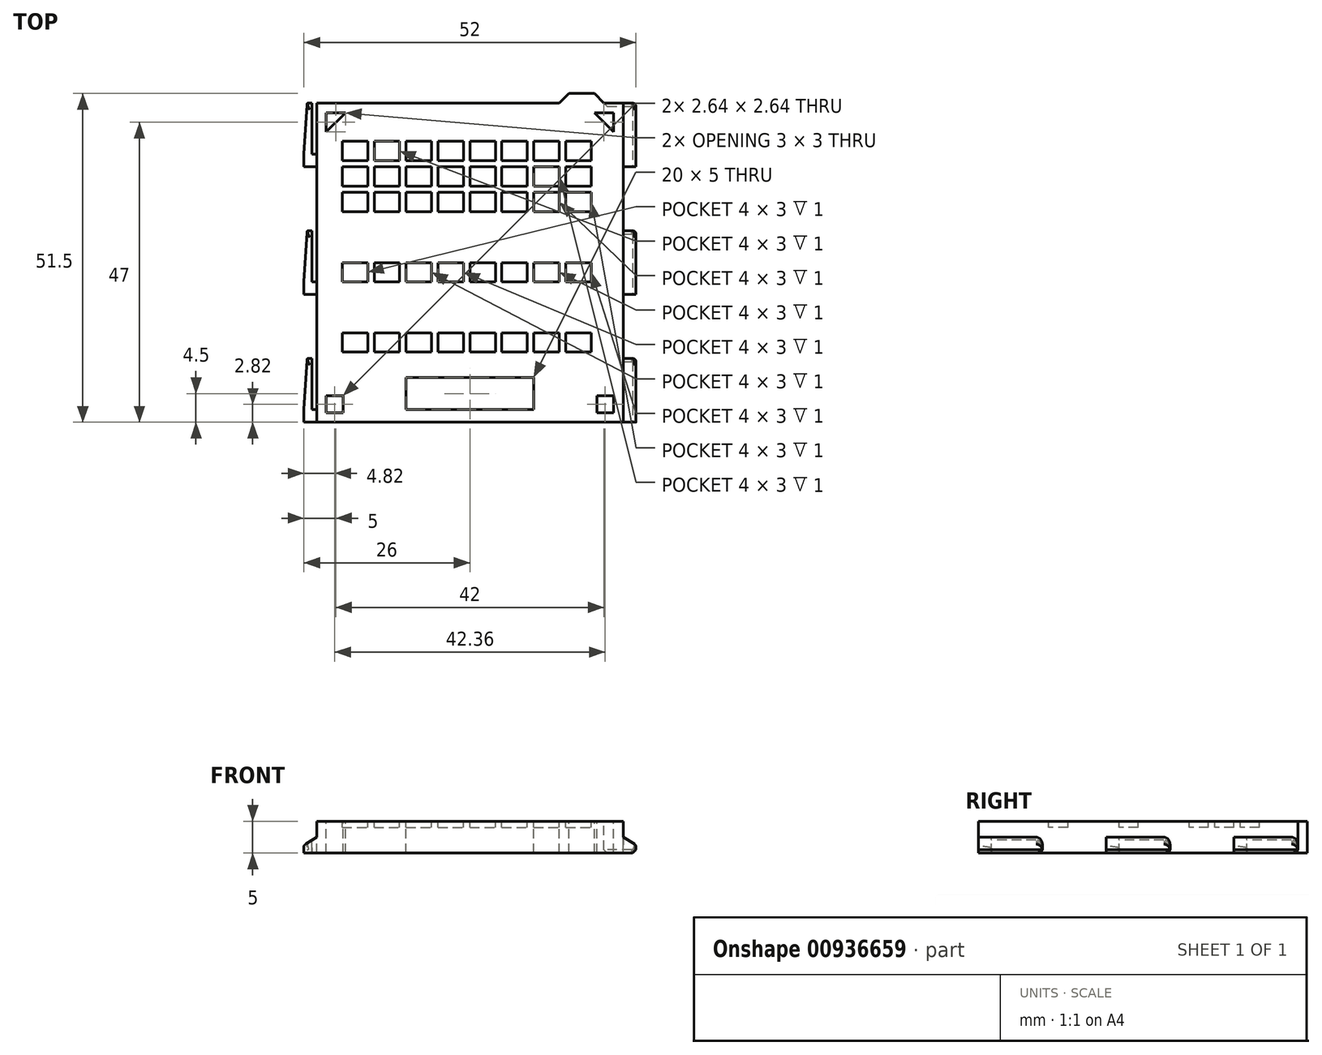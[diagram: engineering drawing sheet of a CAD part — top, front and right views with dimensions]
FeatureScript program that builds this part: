
annotation { "Feature Type Name" : "Feature", "Feature Type Description" : "" }
export const myFeature = defineFeature(function(context is Context, id is Id, definition is map)
    precondition{}
    {
        {
            var Q0;
            Q0=qCreatedBy(makeId("Top.planeOp"),FACE);
            var sketch = newSketch(context, id + "F0", { "sketchPlane" : qUnion([Q0])});
            skLineSegment(sketch, "E0.bottom", {"start": v(0, 0) * mm, "end": v(48, 0) * mm});
            skLineSegment(sketch, "E0.top", {"start": v(0, -50) * mm, "end": v(48, -50) * mm});
            skLineSegment(sketch, "E0.left", {"start": v(0, 0) * mm, "end": v(0, -50) * mm});
            skLineSegment(sketch, "E0.right", {"start": v(48, 0) * mm, "end": v(48, -50) * mm});
            skSolve(sketch);
        }
        {
            var Q0;
            Q0=makeQuery(id+"F0.imprint","IMPRINT",FACE,{"disambiguationData":[TD([[makeQuery(id+"F0.imprint","IMPRINT",EDGE,{"derivedFrom":sQuery(id+"F0.wireOp",EDGE,"E0.bottom")}),-1.0]])]});
            extrude(context, id + "F1", {"entities" : qUnion([Q0]), "depth" : 5 * mm, "offsetDistance" : 25 * mm});
        }
        {
            var Q0;
            Q0=makeQuery(id+"F1.opExtrude","CAP_FACE",FACE,{"disambiguationData":[OSD([sQuery(id+"F0.wireOp",EDGE,"E0.bottom"),sQuery(id+"F0.wireOp",EDGE,"E0.top"),sQuery(id+"F0.wireOp",EDGE,"E0.left"),sQuery(id+"F0.wireOp",EDGE,"E0.right")])],"isStart":false});
            var sketch = newSketch(context, id + "F2", { "sketchPlane" : qUnion([Q0])});
            skLineSegment(sketch, "E1.bottom", {"start": v(4, -6) * mm, "end": v(8, -6) * mm});
            skLineSegment(sketch, "E1.top", {"start": v(4, -9) * mm, "end": v(8, -9) * mm});
            skLineSegment(sketch, "E1.left", {"start": v(4, -6) * mm, "end": v(4, -9) * mm});
            skLineSegment(sketch, "E1.right", {"start": v(8, -6) * mm, "end": v(8, -9) * mm});
            skLineSegment(sketch, "E2.0.1.0", {"start": v(4, -13) * mm, "end": v(8, -13) * mm});
            skLineSegment(sketch, "E2.0.1.1", {"start": v(8, -10) * mm, "end": v(8, -13) * mm});
            skLineSegment(sketch, "E2.0.1.2", {"start": v(4, -10) * mm, "end": v(4, -13) * mm});
            skLineSegment(sketch, "E2.0.1.3", {"start": v(4, -10) * mm, "end": v(8, -10) * mm});
            skLineSegment(sketch, "E2.0.2.0", {"start": v(4, -17) * mm, "end": v(8, -17) * mm});
            skLineSegment(sketch, "E2.0.2.1", {"start": v(8, -14) * mm, "end": v(8, -17) * mm});
            skLineSegment(sketch, "E2.0.2.2", {"start": v(4, -14) * mm, "end": v(4, -17) * mm});
            skLineSegment(sketch, "E2.0.2.3", {"start": v(4, -14) * mm, "end": v(8, -14) * mm});
            skLineSegment(sketch, "E2.1.0.0", {"start": v(9, -9) * mm, "end": v(13, -9) * mm});
            skLineSegment(sketch, "E2.1.0.1", {"start": v(13, -6) * mm, "end": v(13, -9) * mm});
            skLineSegment(sketch, "E2.1.0.2", {"start": v(9, -6) * mm, "end": v(9, -9) * mm});
            skLineSegment(sketch, "E2.1.0.3", {"start": v(9, -6) * mm, "end": v(13, -6) * mm});
            skLineSegment(sketch, "E2.1.1.0", {"start": v(9, -13) * mm, "end": v(13, -13) * mm});
            skLineSegment(sketch, "E2.1.1.1", {"start": v(13, -10) * mm, "end": v(13, -13) * mm});
            skLineSegment(sketch, "E2.1.1.2", {"start": v(9, -10) * mm, "end": v(9, -13) * mm});
            skLineSegment(sketch, "E2.1.1.3", {"start": v(9, -10) * mm, "end": v(13, -10) * mm});
            skLineSegment(sketch, "E2.1.2.0", {"start": v(9, -17) * mm, "end": v(13, -17) * mm});
            skLineSegment(sketch, "E2.1.2.1", {"start": v(13, -14) * mm, "end": v(13, -17) * mm});
            skLineSegment(sketch, "E2.1.2.2", {"start": v(9, -14) * mm, "end": v(9, -17) * mm});
            skLineSegment(sketch, "E2.1.2.3", {"start": v(9, -14) * mm, "end": v(13, -14) * mm});
            skLineSegment(sketch, "E2.2.0.0", {"start": v(14, -9) * mm, "end": v(18, -9) * mm});
            skLineSegment(sketch, "E2.2.0.1", {"start": v(18, -6) * mm, "end": v(18, -9) * mm});
            skLineSegment(sketch, "E2.2.0.2", {"start": v(14, -6) * mm, "end": v(14, -9) * mm});
            skLineSegment(sketch, "E2.2.0.3", {"start": v(14, -6) * mm, "end": v(18, -6) * mm});
            skLineSegment(sketch, "E2.2.1.0", {"start": v(14, -13) * mm, "end": v(18, -13) * mm});
            skLineSegment(sketch, "E2.2.1.1", {"start": v(18, -10) * mm, "end": v(18, -13) * mm});
            skLineSegment(sketch, "E2.2.1.2", {"start": v(14, -10) * mm, "end": v(14, -13) * mm});
            skLineSegment(sketch, "E2.2.1.3", {"start": v(14, -10) * mm, "end": v(18, -10) * mm});
            skLineSegment(sketch, "E2.2.2.0", {"start": v(14, -17) * mm, "end": v(18, -17) * mm});
            skLineSegment(sketch, "E2.2.2.1", {"start": v(18, -14) * mm, "end": v(18, -17) * mm});
            skLineSegment(sketch, "E2.2.2.2", {"start": v(14, -14) * mm, "end": v(14, -17) * mm});
            skLineSegment(sketch, "E2.2.2.3", {"start": v(14, -14) * mm, "end": v(18, -14) * mm});
            skLineSegment(sketch, "E2.3.0.0", {"start": v(19, -9) * mm, "end": v(23, -9) * mm});
            skLineSegment(sketch, "E2.3.0.1", {"start": v(23, -6) * mm, "end": v(23, -9) * mm});
            skLineSegment(sketch, "E2.3.0.2", {"start": v(19, -6) * mm, "end": v(19, -9) * mm});
            skLineSegment(sketch, "E2.3.0.3", {"start": v(19, -6) * mm, "end": v(23, -6) * mm});
            skLineSegment(sketch, "E2.3.1.0", {"start": v(19, -13) * mm, "end": v(23, -13) * mm});
            skLineSegment(sketch, "E2.3.1.1", {"start": v(23, -10) * mm, "end": v(23, -13) * mm});
            skLineSegment(sketch, "E2.3.1.2", {"start": v(19, -10) * mm, "end": v(19, -13) * mm});
            skLineSegment(sketch, "E2.3.1.3", {"start": v(19, -10) * mm, "end": v(23, -10) * mm});
            skLineSegment(sketch, "E2.3.2.0", {"start": v(19, -17) * mm, "end": v(23, -17) * mm});
            skLineSegment(sketch, "E2.3.2.1", {"start": v(23, -14) * mm, "end": v(23, -17) * mm});
            skLineSegment(sketch, "E2.3.2.2", {"start": v(19, -14) * mm, "end": v(19, -17) * mm});
            skLineSegment(sketch, "E2.3.2.3", {"start": v(19, -14) * mm, "end": v(23, -14) * mm});
            skLineSegment(sketch, "E2.4.0.0", {"start": v(24, -9) * mm, "end": v(28, -9) * mm});
            skLineSegment(sketch, "E2.4.0.1", {"start": v(28, -6) * mm, "end": v(28, -9) * mm});
            skLineSegment(sketch, "E2.4.0.2", {"start": v(24, -6) * mm, "end": v(24, -9) * mm});
            skLineSegment(sketch, "E2.4.0.3", {"start": v(24, -6) * mm, "end": v(28, -6) * mm});
            skLineSegment(sketch, "E2.4.1.0", {"start": v(24, -13) * mm, "end": v(28, -13) * mm});
            skLineSegment(sketch, "E2.4.1.1", {"start": v(28, -10) * mm, "end": v(28, -13) * mm});
            skLineSegment(sketch, "E2.4.1.2", {"start": v(24, -10) * mm, "end": v(24, -13) * mm});
            skLineSegment(sketch, "E2.4.1.3", {"start": v(24, -10) * mm, "end": v(28, -10) * mm});
            skLineSegment(sketch, "E2.4.2.0", {"start": v(24, -17) * mm, "end": v(28, -17) * mm});
            skLineSegment(sketch, "E2.4.2.1", {"start": v(28, -14) * mm, "end": v(28, -17) * mm});
            skLineSegment(sketch, "E2.4.2.2", {"start": v(24, -14) * mm, "end": v(24, -17) * mm});
            skLineSegment(sketch, "E2.4.2.3", {"start": v(24, -14) * mm, "end": v(28, -14) * mm});
            skLineSegment(sketch, "E2.5.0.0", {"start": v(29, -9) * mm, "end": v(33, -9) * mm});
            skLineSegment(sketch, "E2.5.0.1", {"start": v(33, -6) * mm, "end": v(33, -9) * mm});
            skLineSegment(sketch, "E2.5.0.2", {"start": v(29, -6) * mm, "end": v(29, -9) * mm});
            skLineSegment(sketch, "E2.5.0.3", {"start": v(29, -6) * mm, "end": v(33, -6) * mm});
            skLineSegment(sketch, "E2.5.1.0", {"start": v(29, -13) * mm, "end": v(33, -13) * mm});
            skLineSegment(sketch, "E2.5.1.1", {"start": v(33, -10) * mm, "end": v(33, -13) * mm});
            skLineSegment(sketch, "E2.5.1.2", {"start": v(29, -10) * mm, "end": v(29, -13) * mm});
            skLineSegment(sketch, "E2.5.1.3", {"start": v(29, -10) * mm, "end": v(33, -10) * mm});
            skLineSegment(sketch, "E2.5.2.0", {"start": v(29, -17) * mm, "end": v(33, -17) * mm});
            skLineSegment(sketch, "E2.5.2.1", {"start": v(33, -14) * mm, "end": v(33, -17) * mm});
            skLineSegment(sketch, "E2.5.2.2", {"start": v(29, -14) * mm, "end": v(29, -17) * mm});
            skLineSegment(sketch, "E2.5.2.3", {"start": v(29, -14) * mm, "end": v(33, -14) * mm});
            skLineSegment(sketch, "E2.direction1", {"start": v(4, -9) * mm, "end": v(9, -9) * mm, "construction": true});
            skLineSegment(sketch, "E2.direction2", {"start": v(4, -9) * mm, "end": v(4, -13) * mm, "construction": true});
            skLineSegment(sketch, "E3.0.6.0", {"start": v(34, -9) * mm, "end": v(38, -9) * mm});
            skLineSegment(sketch, "E3.3.6.0", {"start": v(38, -6) * mm, "end": v(38, -9) * mm});
            skLineSegment(sketch, "E3.6.6.0", {"start": v(34, -6) * mm, "end": v(34, -9) * mm});
            skLineSegment(sketch, "E3.9.6.0", {"start": v(34, -6) * mm, "end": v(38, -6) * mm});
            skLineSegment(sketch, "E3.0.6.1", {"start": v(34, -13) * mm, "end": v(38, -13) * mm});
            skLineSegment(sketch, "E3.3.6.1", {"start": v(38, -10) * mm, "end": v(38, -13) * mm});
            skLineSegment(sketch, "E3.6.6.1", {"start": v(34, -10) * mm, "end": v(34, -13) * mm});
            skLineSegment(sketch, "E3.9.6.1", {"start": v(34, -10) * mm, "end": v(38, -10) * mm});
            skLineSegment(sketch, "E3.0.6.2", {"start": v(34, -17) * mm, "end": v(38, -17) * mm});
            skLineSegment(sketch, "E3.3.6.2", {"start": v(38, -14) * mm, "end": v(38, -17) * mm});
            skLineSegment(sketch, "E3.6.6.2", {"start": v(34, -14) * mm, "end": v(34, -17) * mm});
            skLineSegment(sketch, "E3.9.6.2", {"start": v(34, -14) * mm, "end": v(38, -14) * mm});
            skLineSegment(sketch, "E4.0.7.0", {"start": v(39, -9) * mm, "end": v(43, -9) * mm});
            skLineSegment(sketch, "E4.3.7.0", {"start": v(43, -6) * mm, "end": v(43, -9) * mm});
            skLineSegment(sketch, "E4.6.7.0", {"start": v(39, -6) * mm, "end": v(39, -9) * mm});
            skLineSegment(sketch, "E4.9.7.0", {"start": v(39, -6) * mm, "end": v(43, -6) * mm});
            skLineSegment(sketch, "E4.0.7.1", {"start": v(39, -13) * mm, "end": v(43, -13) * mm});
            skLineSegment(sketch, "E4.3.7.1", {"start": v(43, -10) * mm, "end": v(43, -13) * mm});
            skLineSegment(sketch, "E4.6.7.1", {"start": v(39, -10) * mm, "end": v(39, -13) * mm});
            skLineSegment(sketch, "E4.9.7.1", {"start": v(39, -10) * mm, "end": v(43, -10) * mm});
            skLineSegment(sketch, "E4.0.7.2", {"start": v(39, -17) * mm, "end": v(43, -17) * mm});
            skLineSegment(sketch, "E4.3.7.2", {"start": v(43, -14) * mm, "end": v(43, -17) * mm});
            skLineSegment(sketch, "E4.6.7.2", {"start": v(39, -14) * mm, "end": v(39, -17) * mm});
            skLineSegment(sketch, "E4.9.7.2", {"start": v(39, -14) * mm, "end": v(43, -14) * mm});
            skLineSegment(sketch, "E5.bottom", {"start": v(4, -25) * mm, "end": v(8, -25) * mm});
            skLineSegment(sketch, "E5.top", {"start": v(4, -28) * mm, "end": v(8, -28) * mm});
            skLineSegment(sketch, "E5.left", {"start": v(4, -25) * mm, "end": v(4, -28) * mm});
            skLineSegment(sketch, "E5.right", {"start": v(8, -25) * mm, "end": v(8, -28) * mm});
            skLineSegment(sketch, "E6.1.0.0", {"start": v(9, -25) * mm, "end": v(13, -25) * mm});
            skLineSegment(sketch, "E6.1.0.1", {"start": v(13, -25) * mm, "end": v(13, -28) * mm});
            skLineSegment(sketch, "E6.1.0.2", {"start": v(9, -28) * mm, "end": v(13, -28) * mm});
            skLineSegment(sketch, "E6.1.0.3", {"start": v(9, -25) * mm, "end": v(9, -28) * mm});
            skLineSegment(sketch, "E6.2.0.0", {"start": v(14, -25) * mm, "end": v(18, -25) * mm});
            skLineSegment(sketch, "E6.2.0.1", {"start": v(18, -25) * mm, "end": v(18, -28) * mm});
            skLineSegment(sketch, "E6.2.0.2", {"start": v(14, -28) * mm, "end": v(18, -28) * mm});
            skLineSegment(sketch, "E6.2.0.3", {"start": v(14, -25) * mm, "end": v(14, -28) * mm});
            skLineSegment(sketch, "E6.3.0.0", {"start": v(19, -25) * mm, "end": v(23, -25) * mm});
            skLineSegment(sketch, "E6.3.0.1", {"start": v(23, -25) * mm, "end": v(23, -28) * mm});
            skLineSegment(sketch, "E6.3.0.2", {"start": v(19, -28) * mm, "end": v(23, -28) * mm});
            skLineSegment(sketch, "E6.3.0.3", {"start": v(19, -25) * mm, "end": v(19, -28) * mm});
            skLineSegment(sketch, "E6.4.0.0", {"start": v(24, -25) * mm, "end": v(28, -25) * mm});
            skLineSegment(sketch, "E6.4.0.1", {"start": v(28, -25) * mm, "end": v(28, -28) * mm});
            skLineSegment(sketch, "E6.4.0.2", {"start": v(24, -28) * mm, "end": v(28, -28) * mm});
            skLineSegment(sketch, "E6.4.0.3", {"start": v(24, -25) * mm, "end": v(24, -28) * mm});
            skLineSegment(sketch, "E6.5.0.0", {"start": v(29, -25) * mm, "end": v(33, -25) * mm});
            skLineSegment(sketch, "E6.5.0.1", {"start": v(33, -25) * mm, "end": v(33, -28) * mm});
            skLineSegment(sketch, "E6.5.0.2", {"start": v(29, -28) * mm, "end": v(33, -28) * mm});
            skLineSegment(sketch, "E6.5.0.3", {"start": v(29, -25) * mm, "end": v(29, -28) * mm});
            skLineSegment(sketch, "E6.6.0.0", {"start": v(34, -25) * mm, "end": v(38, -25) * mm});
            skLineSegment(sketch, "E6.6.0.1", {"start": v(38, -25) * mm, "end": v(38, -28) * mm});
            skLineSegment(sketch, "E6.6.0.2", {"start": v(34, -28) * mm, "end": v(38, -28) * mm});
            skLineSegment(sketch, "E6.6.0.3", {"start": v(34, -25) * mm, "end": v(34, -28) * mm});
            skLineSegment(sketch, "E6.7.0.0", {"start": v(39, -25) * mm, "end": v(43, -25) * mm});
            skLineSegment(sketch, "E6.7.0.1", {"start": v(43, -25) * mm, "end": v(43, -28) * mm});
            skLineSegment(sketch, "E6.7.0.2", {"start": v(39, -28) * mm, "end": v(43, -28) * mm});
            skLineSegment(sketch, "E6.7.0.3", {"start": v(39, -25) * mm, "end": v(39, -28) * mm});
            skLineSegment(sketch, "E6.direction1", {"start": v(4, -25) * mm, "end": v(9, -25) * mm, "construction": true});
            skLineSegment(sketch, "E7.bottom", {"start": v(4, -36) * mm, "end": v(8, -36) * mm});
            skLineSegment(sketch, "E7.top", {"start": v(4, -39) * mm, "end": v(8, -39) * mm});
            skLineSegment(sketch, "E7.left", {"start": v(4, -36) * mm, "end": v(4, -39) * mm});
            skLineSegment(sketch, "E7.right", {"start": v(8, -36) * mm, "end": v(8, -39) * mm});
            skLineSegment(sketch, "E8.1.0.0", {"start": v(9, -36) * mm, "end": v(13, -36) * mm});
            skLineSegment(sketch, "E8.1.0.1", {"start": v(13, -36) * mm, "end": v(13, -39) * mm});
            skLineSegment(sketch, "E8.1.0.2", {"start": v(9, -39) * mm, "end": v(13, -39) * mm});
            skLineSegment(sketch, "E8.1.0.3", {"start": v(9, -36) * mm, "end": v(9, -39) * mm});
            skLineSegment(sketch, "E8.2.0.0", {"start": v(14, -36) * mm, "end": v(18, -36) * mm});
            skLineSegment(sketch, "E8.2.0.1", {"start": v(18, -36) * mm, "end": v(18, -39) * mm});
            skLineSegment(sketch, "E8.2.0.2", {"start": v(14, -39) * mm, "end": v(18, -39) * mm});
            skLineSegment(sketch, "E8.2.0.3", {"start": v(14, -36) * mm, "end": v(14, -39) * mm});
            skLineSegment(sketch, "E8.3.0.0", {"start": v(19, -36) * mm, "end": v(23, -36) * mm});
            skLineSegment(sketch, "E8.3.0.1", {"start": v(23, -36) * mm, "end": v(23, -39) * mm});
            skLineSegment(sketch, "E8.3.0.2", {"start": v(19, -39) * mm, "end": v(23, -39) * mm});
            skLineSegment(sketch, "E8.3.0.3", {"start": v(19, -36) * mm, "end": v(19, -39) * mm});
            skLineSegment(sketch, "E8.4.0.0", {"start": v(24, -36) * mm, "end": v(28, -36) * mm});
            skLineSegment(sketch, "E8.4.0.1", {"start": v(28, -36) * mm, "end": v(28, -39) * mm});
            skLineSegment(sketch, "E8.4.0.2", {"start": v(24, -39) * mm, "end": v(28, -39) * mm});
            skLineSegment(sketch, "E8.4.0.3", {"start": v(24, -36) * mm, "end": v(24, -39) * mm});
            skLineSegment(sketch, "E8.5.0.0", {"start": v(29, -36) * mm, "end": v(33, -36) * mm});
            skLineSegment(sketch, "E8.5.0.1", {"start": v(33, -36) * mm, "end": v(33, -39) * mm});
            skLineSegment(sketch, "E8.5.0.2", {"start": v(29, -39) * mm, "end": v(33, -39) * mm});
            skLineSegment(sketch, "E8.5.0.3", {"start": v(29, -36) * mm, "end": v(29, -39) * mm});
            skLineSegment(sketch, "E8.6.0.0", {"start": v(34, -36) * mm, "end": v(38, -36) * mm});
            skLineSegment(sketch, "E8.6.0.1", {"start": v(38, -36) * mm, "end": v(38, -39) * mm});
            skLineSegment(sketch, "E8.6.0.2", {"start": v(34, -39) * mm, "end": v(38, -39) * mm});
            skLineSegment(sketch, "E8.6.0.3", {"start": v(34, -36) * mm, "end": v(34, -39) * mm});
            skLineSegment(sketch, "E8.7.0.0", {"start": v(39, -36) * mm, "end": v(43, -36) * mm});
            skLineSegment(sketch, "E8.7.0.1", {"start": v(43, -36) * mm, "end": v(43, -39) * mm});
            skLineSegment(sketch, "E8.7.0.2", {"start": v(39, -39) * mm, "end": v(43, -39) * mm});
            skLineSegment(sketch, "E8.7.0.3", {"start": v(39, -36) * mm, "end": v(39, -39) * mm});
            skLineSegment(sketch, "E8.direction1", {"start": v(4, -36) * mm, "end": v(9, -36) * mm, "construction": true});
            skSolve(sketch);
        }
        {
            var Q0;
            Q0=makeQuery(id+"F2.imprint","IMPRINT",FACE,{"disambiguationData":[TD([[makeQuery(id+"F2.imprint","IMPRINT",EDGE,{"derivedFrom":sQuery(id+"F2.wireOp",EDGE,"E1.bottom")}),-1.0]])]});
            var Q1;
            Q1=makeQuery(id+"F2.imprint","IMPRINT",FACE,{"disambiguationData":[TD([[makeQuery(id+"F2.imprint","IMPRINT",EDGE,{"derivedFrom":sQuery(id+"F2.wireOp",EDGE,"E2.0.1.0")}),1.0]])]});
            var Q2;
            Q2=makeQuery(id+"F2.imprint","IMPRINT",FACE,{"disambiguationData":[TD([[makeQuery(id+"F2.imprint","IMPRINT",EDGE,{"derivedFrom":sQuery(id+"F2.wireOp",EDGE,"E2.0.2.0")}),1.0]])]});
            var Q3;
            Q3=makeQuery(id+"F2.imprint","IMPRINT",FACE,{"disambiguationData":[TD([[makeQuery(id+"F2.imprint","IMPRINT",EDGE,{"derivedFrom":sQuery(id+"F2.wireOp",EDGE,"E2.0.3.0")}),1.0]])]});
            var Q4;
            Q4=makeQuery(id+"F2.imprint","IMPRINT",FACE,{"disambiguationData":[TD([[makeQuery(id+"F2.imprint","IMPRINT",EDGE,{"derivedFrom":sQuery(id+"F2.wireOp",EDGE,"E2.2.0.0")}),1.0]])]});
            var Q5;
            Q5=makeQuery(id+"F2.imprint","IMPRINT",FACE,{"disambiguationData":[TD([[makeQuery(id+"F2.imprint","IMPRINT",EDGE,{"derivedFrom":sQuery(id+"F2.wireOp",EDGE,"E2.2.1.0")}),1.0]])]});
            var Q6;
            Q6=makeQuery(id+"F2.imprint","IMPRINT",FACE,{"disambiguationData":[TD([[makeQuery(id+"F2.imprint","IMPRINT",EDGE,{"derivedFrom":sQuery(id+"F2.wireOp",EDGE,"E2.2.2.0")}),1.0]])]});
            var Q7;
            Q7=makeQuery(id+"F2.imprint","IMPRINT",FACE,{"disambiguationData":[TD([[makeQuery(id+"F2.imprint","IMPRINT",EDGE,{"derivedFrom":sQuery(id+"F2.wireOp",EDGE,"E2.4.3.0")}),1.0]])]});
            var Q8;
            Q8=makeQuery(id+"F2.imprint","IMPRINT",FACE,{"disambiguationData":[TD([[makeQuery(id+"F2.imprint","IMPRINT",EDGE,{"derivedFrom":sQuery(id+"F2.wireOp",EDGE,"E2.4.4.0")}),1.0]])]});
            var Q9;
            Q9=makeQuery(id+"F2.imprint","IMPRINT",FACE,{"disambiguationData":[TD([[makeQuery(id+"F2.imprint","IMPRINT",EDGE,{"derivedFrom":sQuery(id+"F2.wireOp",EDGE,"E2.4.5.0")}),1.0]])]});
            var Q10;
            Q10=makeQuery(id+"F2.imprint","IMPRINT",FACE,{"disambiguationData":[TD([[makeQuery(id+"F2.imprint","IMPRINT",EDGE,{"derivedFrom":sQuery(id+"F2.wireOp",EDGE,"E2.5.0.0")}),1.0]])]});
            var Q11;
            Q11=makeQuery(id+"F2.imprint","IMPRINT",FACE,{"disambiguationData":[TD([[makeQuery(id+"F2.imprint","IMPRINT",EDGE,{"derivedFrom":sQuery(id+"F2.wireOp",EDGE,"E2.5.1.0")}),1.0]])]});
            var Q12;
            Q12=makeQuery(id+"F2.imprint","IMPRINT",FACE,{"disambiguationData":[TD([[makeQuery(id+"F2.imprint","IMPRINT",EDGE,{"derivedFrom":sQuery(id+"F2.wireOp",EDGE,"E2.5.2.0")}),1.0]])]});
            var Q13;
            Q13=makeQuery(id+"F2.imprint","IMPRINT",FACE,{"disambiguationData":[TD([[makeQuery(id+"F2.imprint","IMPRINT",EDGE,{"derivedFrom":sQuery(id+"F2.wireOp",EDGE,"E2.5.5.0")}),1.0]])]});
            var Q14;
            Q14=makeQuery(id+"F2.imprint","IMPRINT",FACE,{"disambiguationData":[TD([[makeQuery(id+"F2.imprint","IMPRINT",EDGE,{"derivedFrom":sQuery(id+"F2.wireOp",EDGE,"E2.5.4.0")}),1.0]])]});
            var Q15;
            Q15=makeQuery(id+"F2.imprint","IMPRINT",FACE,{"disambiguationData":[TD([[makeQuery(id+"F2.imprint","IMPRINT",EDGE,{"derivedFrom":sQuery(id+"F2.wireOp",EDGE,"E2.5.3.0")}),1.0]])]});
            var Q16;
            Q16=makeQuery(id+"F2.imprint","IMPRINT",FACE,{"disambiguationData":[TD([[makeQuery(id+"F2.imprint","IMPRINT",EDGE,{"derivedFrom":sQuery(id+"F2.wireOp",EDGE,"E2.4.2.0")}),1.0]])]});
            var Q17;
            Q17=makeQuery(id+"F2.imprint","IMPRINT",FACE,{"disambiguationData":[TD([[makeQuery(id+"F2.imprint","IMPRINT",EDGE,{"derivedFrom":sQuery(id+"F2.wireOp",EDGE,"E2.4.1.0")}),1.0]])]});
            var Q18;
            Q18=makeQuery(id+"F2.imprint","IMPRINT",FACE,{"disambiguationData":[TD([[makeQuery(id+"F2.imprint","IMPRINT",EDGE,{"derivedFrom":sQuery(id+"F2.wireOp",EDGE,"E2.4.0.0")}),1.0]])]});
            var Q19;
            Q19=makeQuery(id+"F2.imprint","IMPRINT",FACE,{"disambiguationData":[TD([[makeQuery(id+"F2.imprint","IMPRINT",EDGE,{"derivedFrom":sQuery(id+"F2.wireOp",EDGE,"E2.3.5.0")}),1.0]])]});
            var Q20;
            Q20=makeQuery(id+"F2.imprint","IMPRINT",FACE,{"disambiguationData":[TD([[makeQuery(id+"F2.imprint","IMPRINT",EDGE,{"derivedFrom":sQuery(id+"F2.wireOp",EDGE,"E2.3.4.0")}),1.0]])]});
            var Q21;
            Q21=makeQuery(id+"F2.imprint","IMPRINT",FACE,{"disambiguationData":[TD([[makeQuery(id+"F2.imprint","IMPRINT",EDGE,{"derivedFrom":sQuery(id+"F2.wireOp",EDGE,"E2.3.3.0")}),1.0]])]});
            var Q22;
            Q22=makeQuery(id+"F2.imprint","IMPRINT",FACE,{"disambiguationData":[TD([[makeQuery(id+"F2.imprint","IMPRINT",EDGE,{"derivedFrom":sQuery(id+"F2.wireOp",EDGE,"E2.3.2.0")}),1.0]])]});
            var Q23;
            Q23=makeQuery(id+"F2.imprint","IMPRINT",FACE,{"disambiguationData":[TD([[makeQuery(id+"F2.imprint","IMPRINT",EDGE,{"derivedFrom":sQuery(id+"F2.wireOp",EDGE,"E2.3.1.0")}),1.0]])]});
            var Q24;
            Q24=makeQuery(id+"F2.imprint","IMPRINT",FACE,{"disambiguationData":[TD([[makeQuery(id+"F2.imprint","IMPRINT",EDGE,{"derivedFrom":sQuery(id+"F2.wireOp",EDGE,"E2.3.0.0")}),1.0]])]});
            var Q25;
            Q25=makeQuery(id+"F2.imprint","IMPRINT",FACE,{"disambiguationData":[TD([[makeQuery(id+"F2.imprint","IMPRINT",EDGE,{"derivedFrom":sQuery(id+"F2.wireOp",EDGE,"E2.2.5.0")}),1.0]])]});
            var Q26;
            Q26=makeQuery(id+"F2.imprint","IMPRINT",FACE,{"disambiguationData":[TD([[makeQuery(id+"F2.imprint","IMPRINT",EDGE,{"derivedFrom":sQuery(id+"F2.wireOp",EDGE,"E2.2.4.0")}),1.0]])]});
            var Q27;
            Q27=makeQuery(id+"F2.imprint","IMPRINT",FACE,{"disambiguationData":[TD([[makeQuery(id+"F2.imprint","IMPRINT",EDGE,{"derivedFrom":sQuery(id+"F2.wireOp",EDGE,"E2.1.5.0")}),1.0]])]});
            var Q28;
            Q28=makeQuery(id+"F2.imprint","IMPRINT",FACE,{"disambiguationData":[TD([[makeQuery(id+"F2.imprint","IMPRINT",EDGE,{"derivedFrom":sQuery(id+"F2.wireOp",EDGE,"E2.0.5.0")}),1.0]])]});
            var Q29;
            Q29=makeQuery(id+"F2.imprint","IMPRINT",FACE,{"disambiguationData":[TD([[makeQuery(id+"F2.imprint","IMPRINT",EDGE,{"derivedFrom":sQuery(id+"F2.wireOp",EDGE,"E2.0.4.0")}),1.0]])]});
            var Q30;
            Q30=makeQuery(id+"F2.imprint","IMPRINT",FACE,{"disambiguationData":[TD([[makeQuery(id+"F2.imprint","IMPRINT",EDGE,{"derivedFrom":sQuery(id+"F2.wireOp",EDGE,"E2.1.4.0")}),1.0]])]});
            var Q31;
            Q31=makeQuery(id+"F2.imprint","IMPRINT",FACE,{"disambiguationData":[TD([[makeQuery(id+"F2.imprint","IMPRINT",EDGE,{"derivedFrom":sQuery(id+"F2.wireOp",EDGE,"E2.1.3.0")}),1.0]])]});
            var Q32;
            Q32=makeQuery(id+"F2.imprint","IMPRINT",FACE,{"disambiguationData":[TD([[makeQuery(id+"F2.imprint","IMPRINT",EDGE,{"derivedFrom":sQuery(id+"F2.wireOp",EDGE,"E2.2.3.0")}),1.0]])]});
            var Q33;
            Q33=makeQuery(id+"F2.imprint","IMPRINT",FACE,{"disambiguationData":[TD([[makeQuery(id+"F2.imprint","IMPRINT",EDGE,{"derivedFrom":sQuery(id+"F2.wireOp",EDGE,"E2.1.2.0")}),1.0]])]});
            var Q34;
            Q34=makeQuery(id+"F2.imprint","IMPRINT",FACE,{"disambiguationData":[TD([[makeQuery(id+"F2.imprint","IMPRINT",EDGE,{"derivedFrom":sQuery(id+"F2.wireOp",EDGE,"E2.1.1.0")}),1.0]])]});
            var Q35;
            Q35=makeQuery(id+"F2.imprint","IMPRINT",FACE,{"disambiguationData":[TD([[makeQuery(id+"F2.imprint","IMPRINT",EDGE,{"derivedFrom":sQuery(id+"F2.wireOp",EDGE,"E2.1.0.0")}),1.0]])]});
            var Q36;
            Q36=makeQuery(id+"F2.imprint","IMPRINT",FACE,{"disambiguationData":[TD([[makeQuery(id+"F2.imprint","IMPRINT",EDGE,{"derivedFrom":sQuery(id+"F2.wireOp",EDGE,"E3.0.6.2")}),1.0]])]});
            var Q37;
            Q37=makeQuery(id+"F2.imprint","IMPRINT",FACE,{"disambiguationData":[TD([[makeQuery(id+"F2.imprint","IMPRINT",EDGE,{"derivedFrom":sQuery(id+"F2.wireOp",EDGE,"E6.6.0.0")}),-1.0]])]});
            var Q38;
            Q38=makeQuery(id+"F2.imprint","IMPRINT",FACE,{"disambiguationData":[TD([[makeQuery(id+"F2.imprint","IMPRINT",EDGE,{"derivedFrom":sQuery(id+"F2.wireOp",EDGE,"E6.3.0.0")}),-1.0]])]});
            var Q39;
            Q39=makeQuery(id+"F2.imprint","IMPRINT",FACE,{"disambiguationData":[TD([[makeQuery(id+"F2.imprint","IMPRINT",EDGE,{"derivedFrom":sQuery(id+"F2.wireOp",EDGE,"E6.2.0.0")}),-1.0]])]});
            var Q40;
            Q40=makeQuery(id+"F2.imprint","IMPRINT",FACE,{"disambiguationData":[TD([[makeQuery(id+"F2.imprint","IMPRINT",EDGE,{"derivedFrom":sQuery(id+"F2.wireOp",EDGE,"E6.7.0.0")}),-1.0]])]});
            var Q41;
            Q41=makeQuery(id+"F2.imprint","IMPRINT",FACE,{"disambiguationData":[TD([[makeQuery(id+"F2.imprint","IMPRINT",EDGE,{"derivedFrom":sQuery(id+"F2.wireOp",EDGE,"E4.0.7.2")}),1.0]])]});
            var Q42;
            Q42=makeQuery(id+"F2.imprint","IMPRINT",FACE,{"disambiguationData":[TD([[makeQuery(id+"F2.imprint","IMPRINT",EDGE,{"derivedFrom":sQuery(id+"F2.wireOp",EDGE,"E3.0.6.1")}),1.0]])]});
            var Q43;
            Q43=makeQuery(id+"F2.imprint","IMPRINT",FACE,{"disambiguationData":[TD([[makeQuery(id+"F2.imprint","IMPRINT",EDGE,{"derivedFrom":sQuery(id+"F2.wireOp",EDGE,"E4.0.7.1")}),1.0]])]});
            var Q44;
            Q44=makeQuery(id+"F2.imprint","IMPRINT",FACE,{"disambiguationData":[TD([[makeQuery(id+"F2.imprint","IMPRINT",EDGE,{"derivedFrom":sQuery(id+"F2.wireOp",EDGE,"E4.0.7.0")}),1.0]])]});
            var Q45;
            Q45=makeQuery(id+"F2.imprint","IMPRINT",FACE,{"disambiguationData":[TD([[makeQuery(id+"F2.imprint","IMPRINT",EDGE,{"derivedFrom":sQuery(id+"F2.wireOp",EDGE,"E3.0.6.0")}),1.0]])]});
            var Q46;
            Q46=makeQuery(id+"F2.imprint","IMPRINT",FACE,{"disambiguationData":[TD([[makeQuery(id+"F2.imprint","IMPRINT",EDGE,{"derivedFrom":sQuery(id+"F2.wireOp",EDGE,"E6.1.0.0")}),-1.0]])]});
            var Q47;
            Q47=makeQuery(id+"F2.imprint","IMPRINT",FACE,{"disambiguationData":[TD([[makeQuery(id+"F2.imprint","IMPRINT",EDGE,{"derivedFrom":sQuery(id+"F2.wireOp",EDGE,"E5.bottom")}),-1.0]])]});
            var Q48;
            Q48=makeQuery(id+"F2.imprint","IMPRINT",FACE,{"disambiguationData":[TD([[makeQuery(id+"F2.imprint","IMPRINT",EDGE,{"derivedFrom":sQuery(id+"F2.wireOp",EDGE,"E6.4.0.0")}),-1.0]])]});
            var Q49;
            Q49=makeQuery(id+"F2.imprint","IMPRINT",FACE,{"disambiguationData":[TD([[makeQuery(id+"F2.imprint","IMPRINT",EDGE,{"derivedFrom":sQuery(id+"F2.wireOp",EDGE,"E6.5.0.0")}),-1.0]])]});
            var Q50;
            Q50=makeQuery(id+"F2.imprint","IMPRINT",FACE,{"disambiguationData":[TD([[makeQuery(id+"F2.imprint","IMPRINT",EDGE,{"derivedFrom":sQuery(id+"F2.wireOp",EDGE,"E7.bottom")}),-1.0]])]});
            var Q51;
            Q51=makeQuery(id+"F2.imprint","IMPRINT",FACE,{"disambiguationData":[TD([[makeQuery(id+"F2.imprint","IMPRINT",EDGE,{"derivedFrom":sQuery(id+"F2.wireOp",EDGE,"E8.1.0.0")}),-1.0]])]});
            var Q52;
            Q52=makeQuery(id+"F2.imprint","IMPRINT",FACE,{"disambiguationData":[TD([[makeQuery(id+"F2.imprint","IMPRINT",EDGE,{"derivedFrom":sQuery(id+"F2.wireOp",EDGE,"E8.2.0.0")}),-1.0]])]});
            var Q53;
            Q53=makeQuery(id+"F2.imprint","IMPRINT",FACE,{"disambiguationData":[TD([[makeQuery(id+"F2.imprint","IMPRINT",EDGE,{"derivedFrom":sQuery(id+"F2.wireOp",EDGE,"E8.3.0.0")}),-1.0]])]});
            var Q54;
            Q54=makeQuery(id+"F2.imprint","IMPRINT",FACE,{"disambiguationData":[TD([[makeQuery(id+"F2.imprint","IMPRINT",EDGE,{"derivedFrom":sQuery(id+"F2.wireOp",EDGE,"E8.6.0.0")}),-1.0]])]});
            var Q55;
            Q55=makeQuery(id+"F2.imprint","IMPRINT",FACE,{"disambiguationData":[TD([[makeQuery(id+"F2.imprint","IMPRINT",EDGE,{"derivedFrom":sQuery(id+"F2.wireOp",EDGE,"E8.7.0.0")}),-1.0]])]});
            var Q56;
            Q56=makeQuery(id+"F2.imprint","IMPRINT",FACE,{"disambiguationData":[TD([[makeQuery(id+"F2.imprint","IMPRINT",EDGE,{"derivedFrom":sQuery(id+"F2.wireOp",EDGE,"E8.4.0.0")}),-1.0]])]});
            var Q57;
            Q57=makeQuery(id+"F2.imprint","IMPRINT",FACE,{"disambiguationData":[TD([[makeQuery(id+"F2.imprint","IMPRINT",EDGE,{"derivedFrom":sQuery(id+"F2.wireOp",EDGE,"E8.5.0.0")}),-1.0]])]});
            extrude(context, id + "F3", {"entities" : qUnion([Q0, Q1, Q2, Q3, Q4, Q5, Q6, Q7, Q8, Q9, Q10, Q11, Q12, Q13, Q14, Q15, Q16, Q17, Q18, Q19, Q20, Q21, Q22, Q23, Q24, Q25, Q26, Q27, Q28, Q29, Q30, Q31, Q32, Q33, Q34, Q35, Q36, Q37, Q38, Q39, Q40, Q41, Q42, Q43, Q44, Q45, Q46, Q47, Q48, Q49, Q50, Q51, Q52, Q53, Q54, Q55, Q56, Q57]), "operationType" : NewBodyOperationType.REMOVE, "oppositeDirection" : true, "depth" : 1 * mm, "offsetDistance" : 25 * mm});
        }
        {
            var Q0;
            Q0=makeQuery(id+"F1.opExtrude","SWEPT_FACE",FACE,{"disambiguationData":[OSD([sQuery(id+"F0.wireOp",EDGE,"E0.top")])]});
            var sketch = newSketch(context, id + "F4", { "sketchPlane" : qUnion([Q0])});
            skLineSegment(sketch, "E9", {"start": v(0, 0) * mm, "end": v(-2, 0) * mm});
            skLineSegment(sketch, "E10", {"start": v(48, 0) * mm, "end": v(50, 0) * mm});
            skLineSegment(sketch, "E11", {"start": v(50, 0) * mm, "end": v(50, 1.25) * mm});
            skLineSegment(sketch, "E12", {"start": v(50, 1.25) * mm, "end": v(48, 2.5) * mm});
            skLineSegment(sketch, "E13", {"start": v(-2, 0) * mm, "end": v(-2, 1.25) * mm});
            skLineSegment(sketch, "E14", {"start": v(-2, 1.25) * mm, "end": v(0, 2.5) * mm});
            skSolve(sketch);
        }
        {
            var Q0;
            {var subQ6=sQuery(id+"F4.wireOp",EDGE,"E9");Q0=makeQuery(id+"F4.imprint","IMPRINT",FACE,{"disambiguationData":[TD([[makeQuery(id+"F4.imprint","IMPRINT",EDGE,{"derivedFrom":subQ6}),-1.0]])]});}
            var Q1;
            {var subQ1=sQuery(id+"F4.wireOp",EDGE,"E10");Q1=makeQuery(id+"F4.imprint","IMPRINT",FACE,{"disambiguationData":[TD([[makeQuery(id+"F4.imprint","IMPRINT",EDGE,{"derivedFrom":subQ1}),1.0]])]});}
            var Q2;
            Q2=makeQuery(id+"F1.opExtrude","SWEPT_FACE",FACE,{"disambiguationData":[OSD([sQuery(id+"F0.wireOp",EDGE,"E0.bottom")])]});
            extrude(context, id + "F5", {"entities" : qUnion([Q0, Q1]), "operationType" : NewBodyOperationType.ADD, "endBound" : BoundingType.UP_TO_SURFACE, "oppositeDirection" : true, "depth" : 25 * mm, "endBoundEntityFace" : qUnion([Q2]), "offsetDistance" : 25 * mm});
        }
        {
            var Q0;
            Q0=makeQuery(id+"F1.opExtrude","CAP_FACE",FACE,{"disambiguationData":[OSD([sQuery(id+"F0.wireOp",EDGE,"E0.bottom"),sQuery(id+"F0.wireOp",EDGE,"E0.top"),sQuery(id+"F0.wireOp",EDGE,"E0.left"),sQuery(id+"F0.wireOp",EDGE,"E0.right")])],"isStart":false});
            var sketch = newSketch(context, id + "F6", { "sketchPlane" : qUnion([Q0])});
            skPoint(sketch, "E15.firstSnap0", {"position": v(16, -6) * mm});
            skLineSegment(sketch, "E15.bottom", {"start": v(0, -10) * mm, "end": v(-6.52, -10) * mm});
            skLineSegment(sketch, "E15.top", {"start": v(0, -20) * mm, "end": v(-6.52, -20) * mm});
            skLineSegment(sketch, "E15.left", {"start": v(0, -10) * mm, "end": v(0, -20) * mm});
            skLineSegment(sketch, "E15.right", {"start": v(-6.52, -10) * mm, "end": v(-6.52, -20) * mm});
            skLineSegment(sketch, "E16", {"start": v(24, 0) * mm, "end": v(24, 8.51) * mm, "construction": true});
            skLineSegment(sketch, "E17.MirrorCS", {"start": v(48, -10) * mm, "end": v(54.52, -10) * mm});
            skLineSegment(sketch, "E18.MirrorCS", {"start": v(48, -10) * mm, "end": v(48, -20) * mm});
            skLineSegment(sketch, "E19.MirrorCS", {"start": v(48, -20) * mm, "end": v(54.52, -20) * mm});
            skLineSegment(sketch, "E20.MirrorCS", {"start": v(54.52, -10) * mm, "end": v(54.52, -20) * mm});
            skLineSegment(sketch, "E21.0.1.0", {"start": v(-6.52, -30) * mm, "end": v(-6.52, -40) * mm});
            skLineSegment(sketch, "E21.0.1.1", {"start": v(0, -30) * mm, "end": v(-6.52, -30) * mm});
            skLineSegment(sketch, "E21.0.1.2", {"start": v(0, -40) * mm, "end": v(-6.52, -40) * mm});
            skLineSegment(sketch, "E21.0.1.3", {"start": v(0, -30) * mm, "end": v(0, -40) * mm});
            skLineSegment(sketch, "E21.0.1.4", {"start": v(48, -30) * mm, "end": v(54.52, -30) * mm});
            skLineSegment(sketch, "E21.0.1.5", {"start": v(48, -30) * mm, "end": v(48, -40) * mm});
            skLineSegment(sketch, "E21.0.1.6", {"start": v(54.52, -30) * mm, "end": v(54.52, -40) * mm});
            skLineSegment(sketch, "E21.0.1.7", {"start": v(48, -40) * mm, "end": v(54.52, -40) * mm});
            skLineSegment(sketch, "E21.direction1", {"start": v(-6.52, -20) * mm, "end": v(18.48, -20) * mm, "construction": true});
            skLineSegment(sketch, "E21.direction2", {"start": v(-6.52, -20) * mm, "end": v(-6.52, -40) * mm, "construction": true});
            skSolve(sketch);
        }
        {
            var Q0;
            Q0=makeQuery(id+"F6.imprint","IMPRINT",FACE,{"disambiguationData":[TD([[makeQuery(id+"F6.imprint","IMPRINT",EDGE,{"derivedFrom":sQuery(id+"F6.wireOp",EDGE,"E15.bottom")}),1.0]])]});
            var Q1;
            Q1=makeQuery(id+"F6.imprint","IMPRINT",FACE,{"disambiguationData":[TD([[makeQuery(id+"F6.imprint","IMPRINT",EDGE,{"derivedFrom":sQuery(id+"F6.wireOp",EDGE,"E21.0.1.0")}),1.0]])]});
            var Q2;
            Q2=makeQuery(id+"F6.imprint","IMPRINT",FACE,{"disambiguationData":[TD([[makeQuery(id+"F6.imprint","IMPRINT",EDGE,{"derivedFrom":sQuery(id+"F6.wireOp",EDGE,"E21.0.1.4")}),-1.0]])]});
            var Q3;
            Q3=makeQuery(id+"F6.imprint","IMPRINT",FACE,{"disambiguationData":[TD([[makeQuery(id+"F6.imprint","IMPRINT",EDGE,{"derivedFrom":sQuery(id+"F6.wireOp",EDGE,"E17.MirrorCS")}),-1.0]])]});
            extrude(context, id + "F7", {"entities" : qUnion([Q0, Q1, Q2, Q3]), "operationType" : NewBodyOperationType.REMOVE, "oppositeDirection" : true, "depth" : 25 * mm, "offsetDistance" : 25 * mm});
        }
        {
            var Q0;
            Q0=makeQuery(id+"F1.opExtrude","CAP_FACE",FACE,{"disambiguationData":[OSD([sQuery(id+"F0.wireOp",EDGE,"E0.bottom"),sQuery(id+"F0.wireOp",EDGE,"E0.top"),sQuery(id+"F0.wireOp",EDGE,"E0.left"),sQuery(id+"F0.wireOp",EDGE,"E0.right")])],"isStart":false});
            var sketch = newSketch(context, id + "F8", { "sketchPlane" : qUnion([Q0])});
            skLineSegment(sketch, "E22", {"start": v(0, -48) * mm, "end": v(-0.75, -48) * mm});
            skLineSegment(sketch, "E23", {"start": v(-0.75, -48) * mm, "end": v(-0.75, -39.37) * mm});
            skLineSegment(sketch, "E24", {"start": v(-0.75, -39.37) * mm, "end": v(0, -39.37) * mm});
            skLineSegment(sketch, "E25", {"start": v(0, -39.37) * mm, "end": v(0, -48) * mm});
            skLineSegment(sketch, "E26.0.0", {"start": v(0, -40) * mm, "end": v(-1.31, -40) * mm});
            skLineSegment(sketch, "E26.0.1", {"start": v(-2, -40) * mm, "end": v(-2, -50) * mm});
            skLineSegment(sketch, "E26.0.2", {"start": v(-2, -50) * mm, "end": v(0, -50) * mm});
            skLineSegment(sketch, "E26.0.3", {"start": v(0, -50) * mm, "end": v(0, -40) * mm});
            skLineSegment(sketch, "E27", {"start": v(-2, -40) * mm, "end": v(-2, -47.93) * mm});
            skLineSegment(sketch, "E28", {"start": v(-2, -47.93) * mm, "end": v(-1.51, -40.19) * mm});
            skLineSegment(sketch, "E29", {"start": v(-1.5, -40) * mm, "end": v(-2, -40) * mm});
            skPoint(sketch, "E30.newPointA", {"position": v(-1.5, -40) * mm});
            skPoint(sketch, "E30.newPointB", {"position": v(-2, -40) * mm});
            skArc(sketch, "E30.filletArc", {"start": v(-1.31, -40) * mm, "mid": v(-1.45, -40.05) * mm, "end": v(-1.51, -40.19) * mm});
            skLineSegment(sketch, "E31", {"start": v(-1.31, -40) * mm, "end": v(-1.5, -40) * mm});
            skLineSegment(sketch, "E32.0.1.0", {"start": v(0, -28) * mm, "end": v(-0.75, -28) * mm});
            skLineSegment(sketch, "E32.0.1.1", {"start": v(-0.75, -28) * mm, "end": v(-0.75, -19.37) * mm});
            skLineSegment(sketch, "E32.0.1.2", {"start": v(-0.75, -19.37) * mm, "end": v(0, -19.37) * mm});
            skLineSegment(sketch, "E32.0.1.3", {"start": v(0, -19.37) * mm, "end": v(0, -28) * mm});
            skLineSegment(sketch, "E32.0.1.4", {"start": v(-2, -27.93) * mm, "end": v(-1.51, -20.19) * mm});
            skLineSegment(sketch, "E32.0.1.5", {"start": v(-2, -20) * mm, "end": v(-2, -30) * mm});
            skLineSegment(sketch, "E32.0.1.6", {"start": v(-1.5, -20) * mm, "end": v(-2, -20) * mm});
            skLineSegment(sketch, "E32.0.1.7", {"start": v(-1.31, -20) * mm, "end": v(-1.5, -20) * mm});
            skArc(sketch, "E32.0.1.8", {"start": v(-1.31, -20) * mm, "mid": v(-1.45, -20.05) * mm, "end": v(-1.51, -20.19) * mm});
            skLineSegment(sketch, "E32.0.2.0", {"start": v(0, -8) * mm, "end": v(-0.75, -8) * mm});
            skLineSegment(sketch, "E32.0.2.1", {"start": v(-0.75, -8) * mm, "end": v(-0.75, 0.63) * mm});
            skLineSegment(sketch, "E32.0.2.2", {"start": v(-0.75, 0.63) * mm, "end": v(0, 0.63) * mm});
            skLineSegment(sketch, "E32.0.2.3", {"start": v(0, 0.63) * mm, "end": v(0, -8) * mm});
            skLineSegment(sketch, "E32.0.2.4", {"start": v(-2, -7.93) * mm, "end": v(-1.51, -0.19) * mm});
            skLineSegment(sketch, "E32.0.2.5", {"start": v(-2, 0) * mm, "end": v(-2, -10) * mm});
            skLineSegment(sketch, "E32.0.2.6", {"start": v(-1.5, 0) * mm, "end": v(-2, 0) * mm});
            skLineSegment(sketch, "E32.0.2.7", {"start": v(-1.31, 0) * mm, "end": v(-1.5, 0) * mm});
            skArc(sketch, "E32.0.2.8", {"start": v(-1.31, 0) * mm, "mid": v(-1.45, -0.05) * mm, "end": v(-1.51, -0.19) * mm});
            skLineSegment(sketch, "E32.direction1", {"start": v(-0.75, -48) * mm, "end": v(24.25, -48) * mm, "construction": true});
            skLineSegment(sketch, "E32.direction2", {"start": v(-0.75, -48) * mm, "end": v(-0.75, -28) * mm, "construction": true});
            skLineSegment(sketch, "E33", {"start": v(24, 0.28) * mm, "end": v(24, 4.26) * mm, "construction": true});
            skPoint(sketch, "E33.startSnap0", {"position": v(24, 0) * mm});
            skSolve(sketch);
        }
        {
            var Q0;
            {var subQ0=sQuery(id+"F8.wireOp",EDGE,"E22");Q0=makeQuery(id+"F8.imprint","IMPRINT",FACE,{"disambiguationData":[TD([[makeQuery(id+"F8.imprint","IMPRINT",EDGE,{"derivedFrom":subQ0}),-1.0]])]});}
            var Q1;
            {var subQ0=sQuery(id+"F8.wireOp",EDGE,"E28");Q1=makeQuery(id+"F8.imprint","IMPRINT",FACE,{"disambiguationData":[TD([[makeQuery(id+"F8.imprint","IMPRINT",EDGE,{"derivedFrom":subQ0}),1.0]])]});}
            var Q2;
            Q2=makeQuery(id+"F8.imprint","IMPRINT",FACE,{"disambiguationData":[TD([[makeQuery(id+"F8.imprint","IMPRINT",EDGE,{"derivedFrom":sQuery(id+"F8.wireOp",EDGE,"E32.0.1.0")}),-1.0]])]});
            var Q3;
            {var subQ2=sQuery(id+"F8.wireOp",EDGE,"E32.0.1.4");Q3=makeQuery(id+"F8.imprint","IMPRINT",FACE,{"disambiguationData":[TD([[makeQuery(id+"F8.imprint","IMPRINT",EDGE,{"derivedFrom":subQ2}),1.0]])]});}
            var Q4;
            {var subQ2=sQuery(id+"F8.wireOp",EDGE,"E32.0.2.0");Q4=makeQuery(id+"F8.imprint","IMPRINT",FACE,{"disambiguationData":[TD([[makeQuery(id+"F8.imprint","IMPRINT",EDGE,{"derivedFrom":subQ2}),-1.0]])]});}
            var Q5;
            {var subQ2=sQuery(id+"F8.wireOp",EDGE,"E32.0.2.4");Q5=makeQuery(id+"F8.imprint","IMPRINT",FACE,{"disambiguationData":[TD([[makeQuery(id+"F8.imprint","IMPRINT",EDGE,{"derivedFrom":subQ2}),1.0]])]});}
            var Q6;
            Q6=makeQuery(id+"F8.imprint","IMPRINT",FACE,{"disambiguationData":[TD([[makeQuery(id+"F8.imprint","IMPRINT",EDGE,{"derivedFrom":sQuery(id+"F8.wireOp",EDGE,"e722379a-86f4-49ad-8a47-400355817b230.MirrorCS")}),1.0]])]});
            var Q7;
            Q7=makeQuery(id+"F8.imprint","IMPRINT",FACE,{"disambiguationData":[TD([[makeQuery(id+"F8.imprint","IMPRINT",EDGE,{"derivedFrom":sQuery(id+"F8.wireOp",EDGE,"d30c6836-2050-4577-9a9b-d798b92a200c0.MirrorCS")}),1.0]])]});
            var Q8;
            {var subQ2=sQuery(id+"F8.wireOp",EDGE,"4f4df0a9-7241-4b6c-b748-03f40ba930e40.MirrorCS");Q8=makeQuery(id+"F8.imprint","IMPRINT",FACE,{"disambiguationData":[TD([[makeQuery(id+"F8.imprint","IMPRINT",EDGE,{"derivedFrom":subQ2}),-1.0]])]});}
            var Q9;
            {var subQ1=sQuery(id+"F8.wireOp",EDGE,"5faf99e5-6c72-46fc-adc3-d1651bd9a6770.MirrorCS");Q9=makeQuery(id+"F8.imprint","IMPRINT",FACE,{"disambiguationData":[TD([[makeQuery(id+"F8.imprint","IMPRINT",EDGE,{"derivedFrom":subQ1}),-1.0]])]});}
            var Q10;
            Q10=makeQuery(id+"F8.imprint","IMPRINT",FACE,{"disambiguationData":[TD([[makeQuery(id+"F8.imprint","IMPRINT",EDGE,{"derivedFrom":sQuery(id+"F8.wireOp",EDGE,"cc6e77a2-de85-4070-afac-088a45ef221d0.MirrorCS")}),1.0]])]});
            var Q11;
            Q11=makeQuery(id+"F8.imprint","IMPRINT",FACE,{"disambiguationData":[TD([[makeQuery(id+"F8.imprint","IMPRINT",EDGE,{"derivedFrom":sQuery(id+"F8.wireOp",EDGE,"fa48c959-6260-4dcb-aed2-700d904f25cb0.MirrorCS")}),1.0]])]});
            extrude(context, id + "F9", {"entities" : qUnion([Q0, Q1, Q2, Q3, Q4, Q5, Q6, Q7, Q8, Q9, Q10, Q11]), "operationType" : NewBodyOperationType.REMOVE, "oppositeDirection" : true, "depth" : 25 * mm, "offsetDistance" : 25 * mm});
        }
        {
            var Q0;
            Q0=makeQuery(id+"F7.boolean.opBoolean","INTERSECT",EDGE,{"derivedFrom":[makeQuery(id+"F5.opExtrude","SWEPT_FACE",FACE,{"disambiguationData":[OSD([sQuery(id+"F4.wireOp",EDGE,"E14")])]}),makeQuery(id+"F7.opExtrude","SWEPT_FACE",FACE,{"disambiguationData":[OSD([sQuery(id+"F6.wireOp",EDGE,"E21.0.1.2")])]})]});
            var Q1;
            Q1=makeQuery(id+"F7.boolean.opBoolean","INTERSECT",EDGE,{"derivedFrom":[makeQuery(id+"F5.opExtrude","SWEPT_FACE",FACE,{"disambiguationData":[OSD([sQuery(id+"F4.wireOp",EDGE,"E14")])]}),makeQuery(id+"F7.opExtrude","SWEPT_FACE",FACE,{"disambiguationData":[OSD([sQuery(id+"F6.wireOp",EDGE,"E15.top")])]})]});
            var Q2;
            Q2=makeQuery(id+"F5.opExtrude","CAP_EDGE",EDGE,{"disambiguationData":[OSD([sQuery(id+"F4.wireOp",EDGE,"E14")])],"isStart":false});
            var Q3;
            Q3=makeQuery(id+"F5.opExtrude","CAP_EDGE",EDGE,{"disambiguationData":[OSD([sQuery(id+"F4.wireOp",EDGE,"E12")])],"isStart":false});
            var Q4;
            Q4=makeQuery(id+"F7.boolean.opBoolean","INTERSECT",EDGE,{"derivedFrom":[makeQuery(id+"F5.opExtrude","SWEPT_FACE",FACE,{"disambiguationData":[OSD([sQuery(id+"F4.wireOp",EDGE,"E12")])]}),makeQuery(id+"F7.opExtrude","SWEPT_FACE",FACE,{"disambiguationData":[OSD([sQuery(id+"F6.wireOp",EDGE,"E19.MirrorCS")])]})]});
            var Q5;
            Q5=makeQuery(id+"F7.boolean.opBoolean","INTERSECT",EDGE,{"derivedFrom":[makeQuery(id+"F5.opExtrude","SWEPT_FACE",FACE,{"disambiguationData":[OSD([sQuery(id+"F4.wireOp",EDGE,"E12")])]}),makeQuery(id+"F7.opExtrude","SWEPT_FACE",FACE,{"disambiguationData":[OSD([sQuery(id+"F6.wireOp",EDGE,"E21.0.1.7")])]})]});
            fillet(context, id + "F10", {"entities" : qUnion([Q0, Q1, Q2, Q3, Q4, Q5]), "radius" : 1 * mm, "tangentPropagation" : true, "allowEdgeOverflow" : false});
        }
        {
            var Q0;
            Q0=makeQuery(id+"F1.opExtrude","CAP_FACE",FACE,{"disambiguationData":[OSD([sQuery(id+"F0.wireOp",EDGE,"E0.bottom"),sQuery(id+"F0.wireOp",EDGE,"E0.top"),sQuery(id+"F0.wireOp",EDGE,"E0.left"),sQuery(id+"F0.wireOp",EDGE,"E0.right")])],"isStart":false});
            var sketch = newSketch(context, id + "F11", { "sketchPlane" : qUnion([Q0])});
            skLineSegment(sketch, "E34.bottom", {"start": v(14, -43) * mm, "end": v(34, -43) * mm});
            skLineSegment(sketch, "E34.top", {"start": v(14, -48) * mm, "end": v(34, -48) * mm});
            skLineSegment(sketch, "E34.left", {"start": v(14, -43) * mm, "end": v(14, -48) * mm});
            skLineSegment(sketch, "E34.right", {"start": v(34, -43) * mm, "end": v(34, -48) * mm});
            skLineSegment(sketch, "E35", {"start": v(24, -50) * mm, "end": v(24, -40.68) * mm, "construction": true});
            skPoint(sketch, "E36", {"position": v(24, -48) * mm});
            skLineSegment(sketch, "E37", {"start": v(1.5, -1.5) * mm, "end": v(1.5, -4.5) * mm});
            skLineSegment(sketch, "E38", {"start": v(1.5, -4.5) * mm, "end": v(4.5, -1.5) * mm});
            skLineSegment(sketch, "E39", {"start": v(4.5, -1.5) * mm, "end": v(1.5, -1.5) * mm});
            skLineSegment(sketch, "E40", {"start": v(24, 0) * mm, "end": v(24, -11.18) * mm, "construction": true});
            skLineSegment(sketch, "E41.MirrorCS", {"start": v(46.5, -4.5) * mm, "end": v(43.5, -1.5) * mm});
            skLineSegment(sketch, "E42.MirrorCS", {"start": v(46.5, -1.5) * mm, "end": v(46.5, -4.5) * mm});
            skLineSegment(sketch, "E43.MirrorCS", {"start": v(43.5, -1.5) * mm, "end": v(46.5, -1.5) * mm});
            skLineSegment(sketch, "E44", {"start": v(0, -25) * mm, "end": v(9, -25) * mm, "construction": true});
            skLineSegment(sketch, "E45.MirrorCS", {"start": v(1.5, -45.5) * mm, "end": v(4.5, -48.5) * mm});
            skLineSegment(sketch, "E46.MirrorCS", {"start": v(46.5, -45.5) * mm, "end": v(43.5, -48.5) * mm});
            skLineSegment(sketch, "E47.MirrorCS", {"start": v(43.5, -48.5) * mm, "end": v(46.5, -48.5) * mm});
            skLineSegment(sketch, "E48.MirrorCS", {"start": v(46.5, -48.5) * mm, "end": v(46.5, -45.5) * mm});
            skLineSegment(sketch, "E49.MirrorCS", {"start": v(4.5, -48.5) * mm, "end": v(1.5, -48.5) * mm});
            skLineSegment(sketch, "E50.MirrorCS", {"start": v(1.5, -48.5) * mm, "end": v(1.5, -45.5) * mm});
            skLineSegment(sketch, "E51", {"start": v(1.5, -45.5) * mm, "end": v(4.5, -45.5) * mm});
            skLineSegment(sketch, "E52", {"start": v(4.5, -45.5) * mm, "end": v(4.5, -48.5) * mm});
            skLineSegment(sketch, "E53", {"start": v(46.5, -45.5) * mm, "end": v(43.5, -45.5) * mm});
            skLineSegment(sketch, "E54", {"start": v(43.5, -45.5) * mm, "end": v(43.5, -48.5) * mm});
            skLineSegment(sketch, "E55", {"start": v(1.5, -45.86) * mm, "end": v(4.5, -45.86) * mm});
            skLineSegment(sketch, "E56", {"start": v(4.14, -45.5) * mm, "end": v(4.14, -48.5) * mm});
            skLineSegment(sketch, "E57", {"start": v(43.86, -48.5) * mm, "end": v(43.86, -45.5) * mm});
            skLineSegment(sketch, "E58", {"start": v(43.5, -45.86) * mm, "end": v(46.5, -45.86) * mm});
            skSolve(sketch);
        }
        {
            var Q0;
            Q0=makeQuery(id+"F11.imprint","IMPRINT",FACE,{"disambiguationData":[TD([[makeQuery(id+"F11.imprint","IMPRINT",EDGE,{"derivedFrom":sQuery(id+"F11.wireOp",EDGE,"E34.bottom")}),-1.0]])]});
            var Q1;
            Q1=makeQuery(id+"F11.imprint","IMPRINT",FACE,{"disambiguationData":[TD([[makeQuery(id+"F11.imprint","IMPRINT",EDGE,{"derivedFrom":sQuery(id+"F11.wireOp",EDGE,"E41.MirrorCS")}),-1.0]])]});
            var Q2;
            Q2=makeQuery(id+"F11.imprint","IMPRINT",FACE,{"disambiguationData":[TD([[makeQuery(id+"F11.imprint","IMPRINT",EDGE,{"derivedFrom":sQuery(id+"F11.wireOp",EDGE,"E37")}),1.0]])]});
            var Q3;
            Q3=makeQuery(id+"F11.imprint","IMPRINT",FACE,{"disambiguationData":[TD([[makeQuery(id+"F11.imprint","IMPRINT",EDGE,{"derivedFrom":sQuery(id+"F11.wireOp",EDGE,"E45.MirrorCS")}),1.0]])]});
            var Q4;
            Q4=makeQuery(id+"F11.imprint","IMPRINT",FACE,{"disambiguationData":[TD([[makeQuery(id+"F11.imprint","IMPRINT",EDGE,{"derivedFrom":sQuery(id+"F11.wireOp",EDGE,"E46.MirrorCS")}),-1.0]])]});
            var Q5;
            {var subQ3=sQuery(id+"F11.wireOp",EDGE,"E46.MirrorCS");var subQ7=sQuery(id+"F11.wireOp",EDGE,"E58");var subQ9=makeQuery(id+"F11.imprint","INTERSECT",VERTEX,{"derivedFrom":[subQ3,subQ7]});Q5=makeQuery(id+"F11.imprint","IMPRINT",FACE,{"disambiguationData":[TD([[makeQuery(id+"F11.imprint","IMPRINT",EDGE,{"disambiguationData":[TD([[subQ9,-1.0]])],"derivedFrom":subQ3}),1.0]])]});}
            var Q6;
            {var subQ0=sQuery(id+"F11.wireOp",EDGE,"E55");var subQ3=sQuery(id+"F11.wireOp",EDGE,"E45.MirrorCS");var subQ4=makeQuery(id+"F11.imprint","INTERSECT",VERTEX,{"derivedFrom":[subQ3,subQ0]});Q6=makeQuery(id+"F11.imprint","IMPRINT",FACE,{"disambiguationData":[TD([[makeQuery(id+"F11.imprint","IMPRINT",EDGE,{"disambiguationData":[TD([[subQ4,-1.0]])],"derivedFrom":subQ3}),-1.0]])]});}
            extrude(context, id + "F12", {"entities" : qUnion([Q0, Q1, Q2, Q3, Q4, Q5, Q6]), "operationType" : NewBodyOperationType.REMOVE, "oppositeDirection" : true, "depth" : 5 * mm, "offsetDistance" : 25 * mm});
        }
        {
            var Q0;
            {var subQ0=sQuery(id+"F4.wireOp",EDGE,"E12");var subQ1=sQuery(id+"F4.wireOp",EDGE,"E11");var subQ2=sQuery(id+"F0.wireOp",EDGE,"E0.top");Q0=makeQuery(id+"F7.boolean.opBoolean","SPLIT",EDGE,{"disambiguationData":[TD([makeQuery(id+"F1.opExtrude","SWEPT_FACE",FACE,{"disambiguationData":[OSD([subQ2])]})])],"derivedFrom":makeQuery(id+"F5.opExtrude","SWEPT_EDGE",EDGE,{"disambiguationData":[OSD([subQ1,subQ0])]})});}
            var Q1;
            {var subQ0=sQuery(id+"F4.wireOp",EDGE,"E11");var subQ1=sQuery(id+"F4.wireOp",EDGE,"E12");Q1=makeQuery(id+"F7.boolean.opBoolean","SPLIT",EDGE,{"disambiguationData":[TD([makeQuery(id+"F7.opExtrude","SWEPT_FACE",FACE,{"disambiguationData":[OSD([sQuery(id+"F6.wireOp",EDGE,"E19.MirrorCS")])]})])],"derivedFrom":makeQuery(id+"F5.opExtrude","SWEPT_EDGE",EDGE,{"disambiguationData":[OSD([subQ0,subQ1])]})});}
            var Q2;
            {var subQ0=sQuery(id+"F4.wireOp",EDGE,"E11");var subQ1=sQuery(id+"F4.wireOp",EDGE,"E12");Q2=makeQuery(id+"F7.boolean.opBoolean","SPLIT",EDGE,{"disambiguationData":[TD([makeQuery(id+"F1.opExtrude","SWEPT_FACE",FACE,{"disambiguationData":[OSD([sQuery(id+"F0.wireOp",EDGE,"E0.bottom")])]})])],"derivedFrom":makeQuery(id+"F5.opExtrude","SWEPT_EDGE",EDGE,{"disambiguationData":[OSD([subQ0,subQ1])]})});}
            fillet(context, id + "F13", {"entities" : qUnion([Q0, Q1, Q2]), "radius" : 0.5 * mm, "tangentPropagation" : true, "allowEdgeOverflow" : false});
        }
        {
            var Q0;
            Q0=makeQuery(id+"F1.opExtrude","CAP_FACE",FACE,{"disambiguationData":[OSD([sQuery(id+"F0.wireOp",EDGE,"E0.bottom"),sQuery(id+"F0.wireOp",EDGE,"E0.top"),sQuery(id+"F0.wireOp",EDGE,"E0.left"),sQuery(id+"F0.wireOp",EDGE,"E0.right")])],"isStart":false});
            var sketch = newSketch(context, id + "F14", { "sketchPlane" : qUnion([Q0])});
            skLineSegment(sketch, "E59", {"start": v(45, 0) * mm, "end": v(43.5, 1.5) * mm});
            skLineSegment(sketch, "E60", {"start": v(43.5, 1.5) * mm, "end": v(39.5, 1.5) * mm});
            skLineSegment(sketch, "E61", {"start": v(39.5, 1.5) * mm, "end": v(38, 0) * mm});
            skSolve(sketch);
        }
        {
            var Q0;
            {var subQ0=sQuery(id+"F14.wireOp",EDGE,"E59");Q0=makeQuery(id+"F14.imprint","IMPRINT",FACE,{"disambiguationData":[TD([[makeQuery(id+"F14.imprint","IMPRINT",EDGE,{"derivedFrom":subQ0}),1.0]])]});}
            extrude(context, id + "F15", {"entities" : qUnion([Q0]), "operationType" : NewBodyOperationType.ADD, "oppositeDirection" : true, "depth" : 5 * mm, "offsetDistance" : 25 * mm});
        }
        {
            var Q0;
            {var subQ0=sQuery(id+"F4.wireOp",EDGE,"E11");var subQ1=sQuery(id+"F4.wireOp",EDGE,"E10");Q0=makeQuery(id+"F7.boolean.opBoolean","SPLIT",EDGE,{"disambiguationData":[TD([makeQuery(id+"F7.opExtrude","SWEPT_FACE",FACE,{"disambiguationData":[OSD([sQuery(id+"F6.wireOp",EDGE,"E19.MirrorCS")])]})])],"derivedFrom":makeQuery(id+"F5.opExtrude","SWEPT_EDGE",EDGE,{"disambiguationData":[OSD([subQ1,subQ0])]})});}
            var Q1;
            {var subQ4=sQuery(id+"F0.wireOp",EDGE,"E0.bottom");var subQ5=sQuery(id+"F4.wireOp",EDGE,"E11");var subQ6=sQuery(id+"F4.wireOp",EDGE,"E10");Q1=makeQuery(id+"F7.boolean.opBoolean","SPLIT",EDGE,{"disambiguationData":[TD([makeQuery(id+"F1.opExtrude","SWEPT_FACE",FACE,{"disambiguationData":[OSD([subQ4])]})])],"derivedFrom":makeQuery(id+"F5.opExtrude","SWEPT_EDGE",EDGE,{"disambiguationData":[OSD([subQ6,subQ5])]})});}
            var Q2;
            {var subQ2=sQuery(id+"F0.wireOp",EDGE,"E0.top");var subQ4=sQuery(id+"F4.wireOp",EDGE,"E11");var subQ5=sQuery(id+"F4.wireOp",EDGE,"E10");Q2=makeQuery(id+"F7.boolean.opBoolean","SPLIT",EDGE,{"disambiguationData":[TD([makeQuery(id+"F1.opExtrude","SWEPT_FACE",FACE,{"disambiguationData":[OSD([subQ2])]})])],"derivedFrom":makeQuery(id+"F5.opExtrude","SWEPT_EDGE",EDGE,{"disambiguationData":[OSD([subQ5,subQ4])]})});}
            chamfer(context, id + "F16", {"entities" : qUnion([Q0, Q1, Q2]), "width" : 0.5 * mm, "tangentPropagation" : true});
        }
    });
